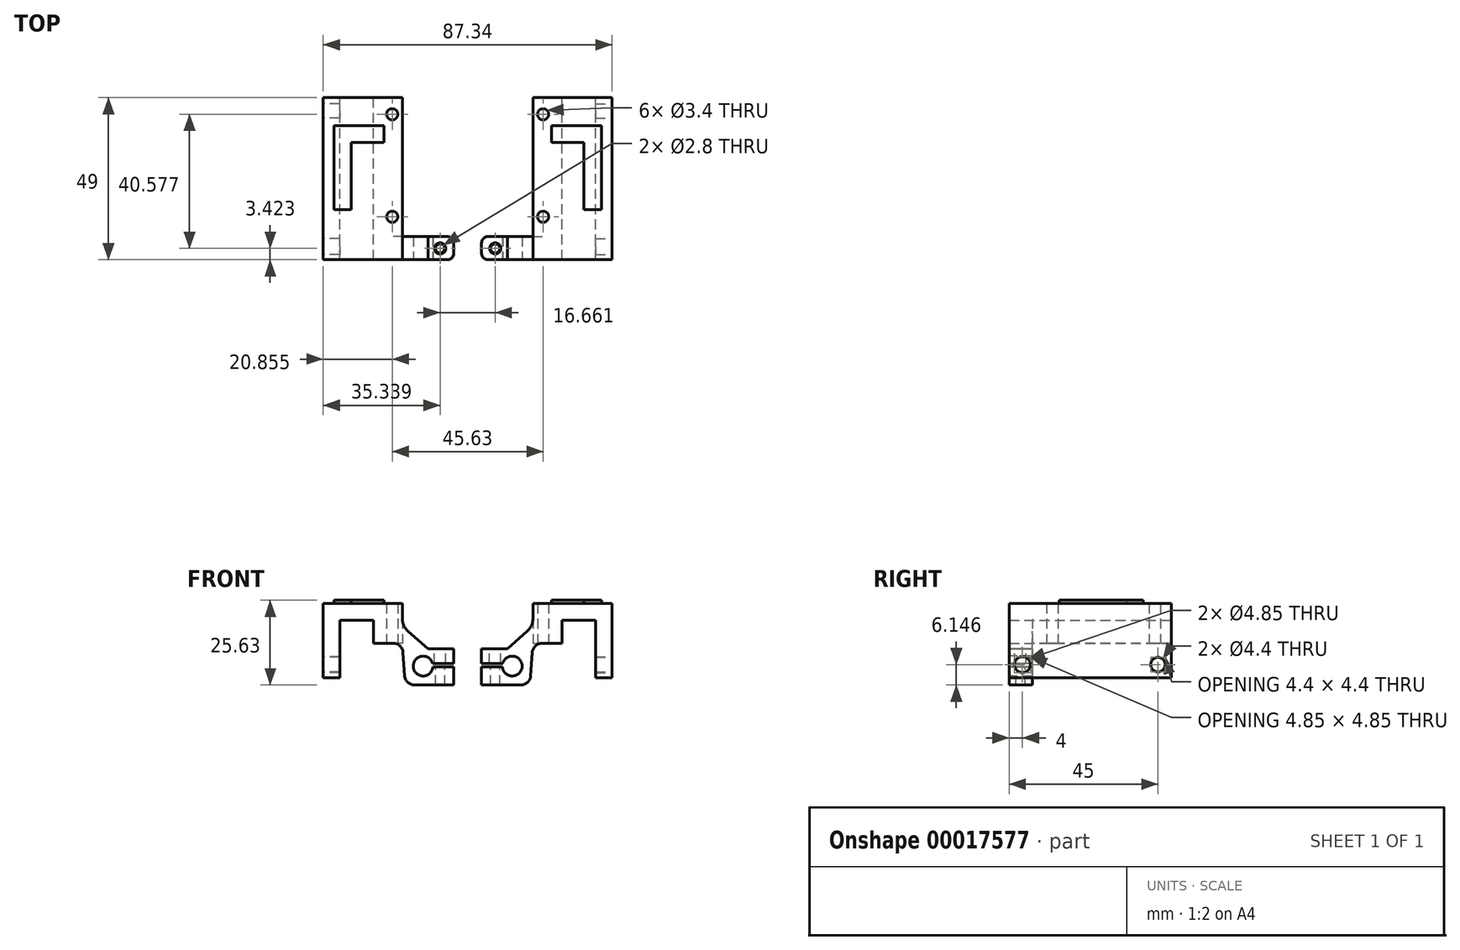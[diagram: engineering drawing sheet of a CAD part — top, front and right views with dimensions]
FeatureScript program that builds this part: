
annotation { "Feature Type Name" : "Feature", "Feature Type Description" : "" }
export const myFeature = defineFeature(function(context is Context, id is Id, definition is map)
    precondition{}
    {
        {
            var Q0;
            Q0=qCreatedBy(makeId("Front.planeOp"),FACE);
            var sketch = newSketch(context, id + "F0", { "sketchPlane" : qUnion([Q0])});
            skLineSegment(sketch, "E0", {"start": v(-18.67, 7.33) * mm, "end": v(-18.67, 29.8) * mm});
            skLineSegment(sketch, "E1", {"start": v(-18.67, 29.8) * mm, "end": v(5.26, 29.8) * mm});
            skLineSegment(sketch, "E2", {"start": v(5.26, 29.8) * mm, "end": v(5.26, 22.94) * mm});
            skLineSegment(sketch, "E3", {"start": v(-3.47, 17.8) * mm, "end": v(-3.47, 24.8) * mm});
            skLineSegment(sketch, "E4", {"start": v(-3.47, 24.8) * mm, "end": v(-13.67, 24.8) * mm});
            skLineSegment(sketch, "E5", {"start": v(-13.67, 24.8) * mm, "end": v(-13.67, 7.33) * mm});
            skLineSegment(sketch, "E6", {"start": v(-13.67, 7.33) * mm, "end": v(-18.67, 7.33) * mm});
            skLineSegment(sketch, "E7", {"start": v(5.26, 22.94) * mm, "end": v(5.26, 17.8) * mm});
            skLineSegment(sketch, "E8", {"start": v(5.26, 17.8) * mm, "end": v(-3.47, 17.8) * mm});
            skLineSegment(sketch, "E9", {"start": v(5.26, 22.94) * mm, "end": v(5.26, 22.94) * mm});
            skLineSegment(sketch, "E10", {"start": v(20.79, 16.13) * mm, "end": v(20.79, 11.7) * mm});
            skLineSegment(sketch, "E11", {"start": v(20.79, 11.7) * mm, "end": v(13.49, 11.7) * mm});
            skLineSegment(sketch, "E12", {"start": v(13.49, 11.7) * mm, "end": v(13.49, 10.67) * mm});
            skLineSegment(sketch, "E13", {"start": v(13.49, 10.67) * mm, "end": v(20.82, 10.67) * mm});
            skLineSegment(sketch, "E14", {"start": v(20.82, 10.67) * mm, "end": v(20.82, 5.18) * mm});
            skLineSegment(sketch, "E15", {"start": v(20.82, 5.18) * mm, "end": v(6.11, 5.18) * mm});
            skLineSegment(sketch, "E16", {"start": v(6.11, 5.18) * mm, "end": v(5.26, 17.8) * mm});
            skLineSegment(sketch, "E17", {"start": v(20.79, 16.13) * mm, "end": v(13, 16.13) * mm});
            skLineSegment(sketch, "E18", {"start": v(13, 16.13) * mm, "end": v(5.26, 22.94) * mm});
            skSolve(sketch);
        }
        {
            var Q0;
            Q0=makeQuery(id+"F0.imprint","IMPRINT",FACE,{"disambiguationData":[TD([[makeQuery(id+"F0.imprint","IMPRINT",EDGE,{"derivedFrom":sQuery(id+"F0.wireOp",EDGE,"E0")}),-1.0]])]});
            var Q1;
            {var subQ2=sQuery(id+"F0.wireOp",EDGE,"69cbcc5d-e0c3-48db-8baf-3487a8abab7d");Q1=makeQuery(id+"F0.imprint","IMPRINT",FACE,{"disambiguationData":[TD([[makeQuery(id+"F0.imprint","IMPRINT",EDGE,{"derivedFrom":subQ2}),-1.0]])]});}
            var Q2;
            Q2=makeQuery(id+"F0.imprint","IMPRINT",FACE,{"disambiguationData":[TD([[makeQuery(id+"F0.imprint","IMPRINT",EDGE,{"derivedFrom":sQuery(id+"F0.wireOp",EDGE,"E7")}),1.0]])]});
            extrude(context, id + "F1", {"entities" : qUnion([Q0, Q1, Q2]), "depth" : 7 * mm});
        }
        {
            var Q0;
            Q0=makeQuery(id+"F0.imprint","IMPRINT",FACE,{"disambiguationData":[TD([[makeQuery(id+"F0.imprint","IMPRINT",EDGE,{"derivedFrom":sQuery(id+"F0.wireOp",EDGE,"E0")}),-1.0]])]});
            extrude(context, id + "F2", {"entities" : qUnion([Q0]), "operationType" : NewBodyOperationType.ADD, "oppositeDirection" : true, "depth" : 42 * mm});
        }
        {
            var Q0;
            {var subQ0=sQuery(id+"F0.wireOp",EDGE,"E8");Q0=makeQuery(id+"F2.boolean.opBoolean","MERGE",FACE,{"derivedFrom":[makeQuery(id+"F1.opExtrude","SWEPT_FACE",FACE,{"disambiguationData":[OSD([subQ0])]}),makeQuery(id+"F2.opExtrude","SWEPT_FACE",FACE,{"disambiguationData":[OSD([subQ0])]})]});}
            var sketch = newSketch(context, id + "F3", { "sketchPlane" : qUnion([Q0])});
            skCircle(sketch, "E19", {"center": v(2.19, -6) * mm, "radius": 1.7 * mm});
            skCircle(sketch, "E20", {"center": v(2.19, -37) * mm, "radius": 1.7 * mm});
            skCircle(sketch, "E21", {"center": v(17.69, -21.5) * mm, "radius": 11 * mm});
            skSolve(sketch);
        }
        {
            var Q0;
            Q0=qSketchRegion(id+"F3",true);
            extrude(context, id + "F4", {"entities" : qUnion([Q0]), "operationType" : NewBodyOperationType.REMOVE, "endBound" : BoundingType.THROUGH_ALL, "oppositeDirection" : true, "depth" : 25 * mm});
        }
        {
            var Q0;
            Q0=makeQuery(id+"F1.opExtrude","CAP_FACE",FACE,{"disambiguationData":[OSD([sQuery(id+"F0.wireOp",EDGE,"E0"),sQuery(id+"F0.wireOp",EDGE,"E1"),sQuery(id+"F0.wireOp",EDGE,"E2"),sQuery(id+"F0.wireOp",EDGE,"E3"),sQuery(id+"F0.wireOp",EDGE,"E4"),sQuery(id+"F0.wireOp",EDGE,"E5"),sQuery(id+"F0.wireOp",EDGE,"E6"),sQuery(id+"F0.wireOp",EDGE,"E8"),sQuery(id+"F0.wireOp",EDGE,"E9"),sQuery(id+"F0.wireOp",EDGE,"58f11638-63e7-4b32-8aff-a1ba3c53649b"),sQuery(id+"F0.wireOp",EDGE,"E10"),sQuery(id+"F0.wireOp",EDGE,"E11"),sQuery(id+"F0.wireOp",EDGE,"E12"),sQuery(id+"F0.wireOp",EDGE,"E13"),sQuery(id+"F0.wireOp",EDGE,"E14"),sQuery(id+"F0.wireOp",EDGE,"E15"),sQuery(id+"F0.wireOp",EDGE,"E16")])],"isStart":false});
            var sketch = newSketch(context, id + "F5", { "sketchPlane" : qUnion([Q0])});
            skCircle(sketch, "E22", {"center": v(11.53, 10.9) * mm, "radius": 3 * mm});
            skSolve(sketch);
        }
        {
            var Q0;
            Q0=qSketchRegion(id+"F5",true);
            extrude(context, id + "F6", {"entities" : qUnion([Q0]), "operationType" : NewBodyOperationType.REMOVE, "oppositeDirection" : true, "depth" : 10 * mm});
        }
        {
            var Q0;
            Q0=qSketchRegion(id+"F3",true);
            extrude(context, id + "F7", {"entities" : qUnion([Q0]), "operationType" : NewBodyOperationType.REMOVE, "endBound" : BoundingType.THROUGH_ALL, "oppositeDirection" : true, "depth" : 25 * mm});
        }
        {
            var Q0;
            Q0=makeQuery(id+"F1.opExtrude","SWEPT_FACE",FACE,{"disambiguationData":[OSD([sQuery(id+"F0.wireOp",EDGE,"E17")])]});
            var sketch = newSketch(context, id + "F8", { "sketchPlane" : qUnion([Q0])});
            skCircle(sketch, "E23", {"center": v(16.67, -3.58) * mm, "radius": 1.7 * mm});
            skCircle(sketch, "E24", {"center": v(16.67, -3.58) * mm, "radius": 1.4 * mm});
            skSolve(sketch);
        }
        {
            var Q0;
            Q0=makeQuery(id+"F8.imprint","IMPRINT",FACE,{"disambiguationData":[TD([[makeQuery(id+"F8.imprint","IMPRINT",EDGE,{"derivedFrom":sQuery(id+"F8.wireOp",EDGE,"E24")}),1.0]])]});
            extrude(context, id + "F9", {"entities" : qUnion([Q0]), "operationType" : NewBodyOperationType.REMOVE, "endBound" : BoundingType.THROUGH_ALL, "oppositeDirection" : true, "depth" : 25 * mm});
        }
        {
            var Q0;
            Q0=makeQuery(id+"F8.imprint","IMPRINT",FACE,{"disambiguationData":[TD([[makeQuery(id+"F8.imprint","IMPRINT",EDGE,{"derivedFrom":sQuery(id+"F8.wireOp",EDGE,"E23")}),1.0]])]});
            extrude(context, id + "F10", {"entities" : qUnion([Q0]), "operationType" : NewBodyOperationType.REMOVE, "endBound" : BoundingType.UP_TO_NEXT, "oppositeDirection" : true, "depth" : 25 * mm});
        }
        {
            var Q0;
            Q0=makeQuery(id+"F1.opExtrude","SWEPT_EDGE",EDGE,{"disambiguationData":[OSD([sQuery(id+"F0.wireOp",EDGE,"E2"),sQuery(id+"F0.wireOp",EDGE,"E7"),sQuery(id+"F0.wireOp",EDGE,"E18")])]});
            fillet(context, id + "F11", {"entities" : qUnion([Q0]), "radius" : 5 * mm, "tangentPropagation" : true, "allowEdgeOverflow" : false});
        }
        {
            var Q0;
            Q0=makeQuery(id+"F1.opExtrude","SWEPT_EDGE",EDGE,{"disambiguationData":[OSD([sQuery(id+"F0.wireOp",EDGE,"E7"),sQuery(id+"F0.wireOp",EDGE,"E8"),sQuery(id+"F0.wireOp",EDGE,"E16")])]});
            fillet(context, id + "F12", {"entities" : qUnion([Q0]), "radius" : 3 * mm, "tangentPropagation" : true, "allowEdgeOverflow" : false});
        }
        {
            var Q0;
            Q0=makeQuery(id+"F1.opExtrude","SWEPT_EDGE",EDGE,{"disambiguationData":[OSD([sQuery(id+"F0.wireOp",EDGE,"E15"),sQuery(id+"F0.wireOp",EDGE,"E16")])]});
            fillet(context, id + "F13", {"entities" : qUnion([Q0]), "radius" : 3 * mm, "tangentPropagation" : true, "allowEdgeOverflow" : false});
        }
        {
            var Q0;
            Q0=makeQuery(id+"F1.opExtrude","CAP_EDGE",EDGE,{"disambiguationData":[OSD([sQuery(id+"F0.wireOp",EDGE,"E10")])],"isStart":false});
            var Q1;
            Q1=makeQuery(id+"F1.opExtrude","CAP_EDGE",EDGE,{"disambiguationData":[OSD([sQuery(id+"F0.wireOp",EDGE,"E14")])],"isStart":false});
            var Q2;
            Q2=makeQuery(id+"F1.opExtrude","CAP_EDGE",EDGE,{"disambiguationData":[OSD([sQuery(id+"F0.wireOp",EDGE,"E10")])],"isStart":true});
            var Q3;
            Q3=makeQuery(id+"F1.opExtrude","CAP_EDGE",EDGE,{"disambiguationData":[OSD([sQuery(id+"F0.wireOp",EDGE,"E14")])],"isStart":true});
            fillet(context, id + "F14", {"entities" : qUnion([Q0, Q1, Q2, Q3]), "radius" : 2 * mm, "tangentPropagation" : true, "allowEdgeOverflow" : false});
        }
        {
            var Q0;
            {var subQ0=sQuery(id+"F0.wireOp",EDGE,"E0");Q0=makeQuery(id+"F2.boolean.opBoolean","MERGE",FACE,{"derivedFrom":[makeQuery(id+"F1.opExtrude","SWEPT_FACE",FACE,{"disambiguationData":[OSD([subQ0])]}),makeQuery(id+"F2.opExtrude","SWEPT_FACE",FACE,{"disambiguationData":[OSD([subQ0])]})]});}
            var sketch = newSketch(context, id + "F15", { "sketchPlane" : qUnion([Q0])});
            skCircle(sketch, "E25", {"center": v(-38, 11.33) * mm, "radius": 2.2 * mm});
            skCircle(sketch, "E26", {"center": v(3, 11.33) * mm, "radius": 2.43 * mm});
            skSolve(sketch);
        }
        {
            var Q0;
            Q0=qSketchRegion(id+"F15",true);
            extrude(context, id + "F16", {"entities" : qUnion([Q0]), "operationType" : NewBodyOperationType.REMOVE, "oppositeDirection" : true, "depth" : 6 * mm});
        }
        {
            var Q0;
            {var subQ0=sQuery(id+"F0.wireOp",EDGE,"E1");Q0=makeQuery(id+"F2.boolean.opBoolean","MERGE",FACE,{"derivedFrom":[makeQuery(id+"F1.opExtrude","SWEPT_FACE",FACE,{"disambiguationData":[OSD([subQ0])]}),makeQuery(id+"F2.opExtrude","SWEPT_FACE",FACE,{"disambiguationData":[OSD([subQ0])]})]});}
            var sketch = newSketch(context, id + "F17", { "sketchPlane" : qUnion([Q0])});
            skLineSegment(sketch, "E27", {"start": v(-10.17, 8.12) * mm, "end": v(-10.17, 28.47) * mm});
            skLineSegment(sketch, "E28", {"start": v(-10.17, 28.47) * mm, "end": v(-0.32, 28.47) * mm});
            skLineSegment(sketch, "E29", {"start": v(-0.32, 28.47) * mm, "end": v(-0.32, 33.49) * mm});
            skLineSegment(sketch, "E30", {"start": v(-15.42, 33.49) * mm, "end": v(-15.42, 8.12) * mm});
            skLineSegment(sketch, "E31", {"start": v(-15.42, 8.12) * mm, "end": v(-10.17, 8.12) * mm});
            skLineSegment(sketch, "E32", {"start": v(-0.32, 33.49) * mm, "end": v(-15.42, 33.49) * mm});
            skSolve(sketch);
        }
        {
            var Q0;
            Q0=qSketchRegion(id+"F17",true);
            extrude(context, id + "F18", {"entities" : qUnion([Q0]), "operationType" : NewBodyOperationType.ADD, "depth" : 1 * mm});
        }
        {
            var Q0;
            Q0=makeQuery(id+"F1.opExtrude","SWEPT_BODY",BODY,{"disambiguationData":[OSD([sQuery(id+"F0.wireOp",EDGE,"E0"),sQuery(id+"F0.wireOp",EDGE,"E1"),sQuery(id+"F0.wireOp",EDGE,"E2"),sQuery(id+"F0.wireOp",EDGE,"E3"),sQuery(id+"F0.wireOp",EDGE,"E4"),sQuery(id+"F0.wireOp",EDGE,"E5"),sQuery(id+"F0.wireOp",EDGE,"E6"),sQuery(id+"F0.wireOp",EDGE,"E8"),sQuery(id+"F0.wireOp",EDGE,"E10"),sQuery(id+"F0.wireOp",EDGE,"E11"),sQuery(id+"F0.wireOp",EDGE,"E12"),sQuery(id+"F0.wireOp",EDGE,"E13"),sQuery(id+"F0.wireOp",EDGE,"E14"),sQuery(id+"F0.wireOp",EDGE,"E15"),sQuery(id+"F0.wireOp",EDGE,"E16"),sQuery(id+"F0.wireOp",EDGE,"E17"),sQuery(id+"F0.wireOp",EDGE,"E18")])]});
            var Q1;
            Q1=qCreatedBy(makeId("Right.planeOp"),FACE);
            mirror(context, id + "F19", {"entities" : qUnion([Q0]), "mirrorPlane" : qUnion([Q1])});
        }
        {
            var Q0;
            Q0=makeQuery(id+"F19.opPattern","COPY",BODY,{"derivedFrom":makeQuery(id+"F1.opExtrude","SWEPT_BODY",BODY,{"disambiguationData":[OSD([sQuery(id+"F0.wireOp",EDGE,"E0"),sQuery(id+"F0.wireOp",EDGE,"E1"),sQuery(id+"F0.wireOp",EDGE,"E2"),sQuery(id+"F0.wireOp",EDGE,"E3"),sQuery(id+"F0.wireOp",EDGE,"E4"),sQuery(id+"F0.wireOp",EDGE,"E5"),sQuery(id+"F0.wireOp",EDGE,"E6"),sQuery(id+"F0.wireOp",EDGE,"E8"),sQuery(id+"F0.wireOp",EDGE,"E10"),sQuery(id+"F0.wireOp",EDGE,"E11"),sQuery(id+"F0.wireOp",EDGE,"E12"),sQuery(id+"F0.wireOp",EDGE,"E13"),sQuery(id+"F0.wireOp",EDGE,"E14"),sQuery(id+"F0.wireOp",EDGE,"E15"),sQuery(id+"F0.wireOp",EDGE,"E16"),sQuery(id+"F0.wireOp",EDGE,"E17"),sQuery(id+"F0.wireOp",EDGE,"E18")])]}),"instanceName":"1"});
            transform(context, id + "F20", {"entities" : qUnion([Q0]), "transformType" : TransformType.TRANSLATION_3D, "dx" : 50 * mm, "dy" : 0 * mm, "dz" : 0 * mm, "makeCopy" : false});
        }
    });
